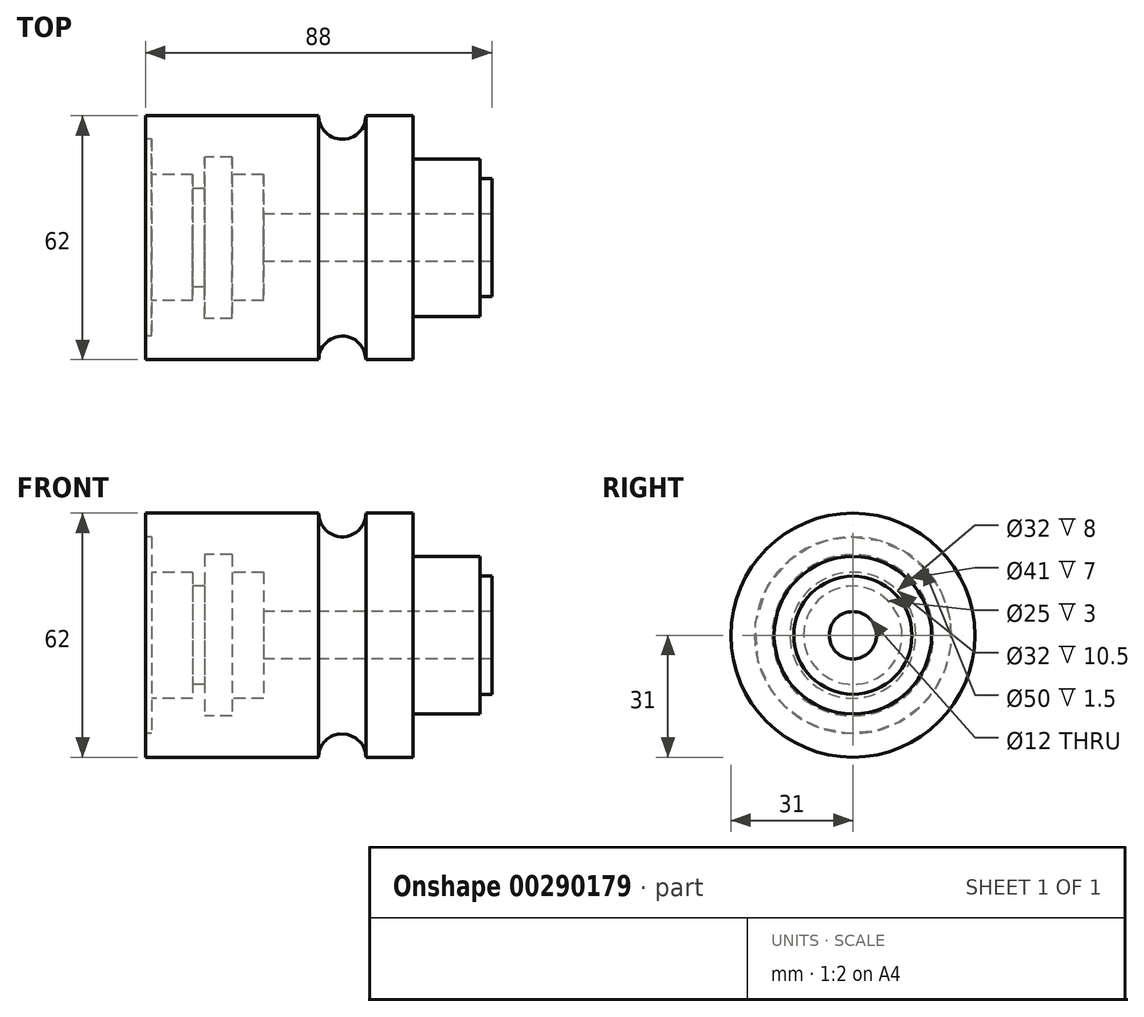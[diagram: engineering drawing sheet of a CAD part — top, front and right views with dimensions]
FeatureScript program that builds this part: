
annotation { "Feature Type Name" : "Feature", "Feature Type Description" : "" }
export const myFeature = defineFeature(function(context is Context, id is Id, definition is map)
    precondition{}
    {
        {
            var Q0;
            Q0=qCreatedBy(makeId("Front.planeOp"),FACE);
            var sketch = newSketch(context, id + "F0", { "sketchPlane" : qUnion([Q0])});
            skLineSegment(sketch, "E0", {"start": v(0, 0) * mm, "end": v(178.14, 0) * mm, "construction": true});
            skLineSegment(sketch, "E1", {"start": v(0, 0) * mm, "end": v(0, 31) * mm});
            skLineSegment(sketch, "E2", {"start": v(0, 31) * mm, "end": v(44, 31) * mm});
            skLineSegment(sketch, "E3", {"start": v(68, 31) * mm, "end": v(68, 20) * mm});
            skLineSegment(sketch, "E4", {"start": v(88, 15) * mm, "end": v(88, 0) * mm});
            skLineSegment(sketch, "E5", {"start": v(88, 0) * mm, "end": v(0, 0) * mm});
            skLineSegment(sketch, "E6", {"start": v(68, 20) * mm, "end": v(85, 20) * mm});
            skLineSegment(sketch, "E7", {"start": v(85, 20) * mm, "end": v(85, 15) * mm});
            skLineSegment(sketch, "E8", {"start": v(85, 15) * mm, "end": v(88, 15) * mm});
            skArc(sketch, "E9", {"start": v(44, 31) * mm, "mid": v(50, 25) * mm, "end": v(56, 31) * mm});
            skLineSegment(sketch, "E10.trimOffspring", {"start": v(56, 31) * mm, "end": v(68, 31) * mm});
            skSolve(sketch);
        }
        {
            var Q0;
            Q0 = qSketchRegion(id + "F0", true);
            var Q1;
            Q1=sQuery(id+"F0.wireOp",EDGE,"E0");
            revolve(context, id + "F1", {"entities" : qUnion([Q0]), "axis" : qUnion([Q1]), "revolveType" : RevolveType.FULL});
        }
        {
            var Q0;
            Q0=qCreatedBy(makeId("Front.planeOp"),FACE);
            var sketch = newSketch(context, id + "F2", { "sketchPlane" : qUnion([Q0])});
            skLineSegment(sketch, "E11", {"start": v(0, 0) * mm, "end": v(0, 25) * mm});
            skLineSegment(sketch, "E12", {"start": v(0, 25) * mm, "end": v(1.5, 25) * mm});
            skLineSegment(sketch, "E13", {"start": v(1.5, 25) * mm, "end": v(1.5, 16) * mm});
            skLineSegment(sketch, "E14", {"start": v(1.5, 16) * mm, "end": v(12, 16) * mm});
            skLineSegment(sketch, "E15", {"start": v(12, 16) * mm, "end": v(12, 12.5) * mm});
            skLineSegment(sketch, "E16", {"start": v(12, 12.5) * mm, "end": v(15, 12.5) * mm});
            skLineSegment(sketch, "E17", {"start": v(22, 16) * mm, "end": v(30, 16) * mm});
            skLineSegment(sketch, "E18", {"start": v(30, 16) * mm, "end": v(30, 6) * mm});
            skLineSegment(sketch, "E19", {"start": v(30, 6) * mm, "end": v(88, 6) * mm});
            skLineSegment(sketch, "E20", {"start": v(88, 6) * mm, "end": v(88, 0) * mm});
            skLineSegment(sketch, "E21", {"start": v(88, 0) * mm, "end": v(0, 0) * mm});
            skLineSegment(sketch, "E22", {"start": v(0, 0) * mm, "end": v(-52.04, 0) * mm, "construction": true});
            skLineSegment(sketch, "E23", {"start": v(15, 12.5) * mm, "end": v(15, 20.5) * mm});
            skLineSegment(sketch, "E24", {"start": v(15, 20.5) * mm, "end": v(22, 20.5) * mm});
            skLineSegment(sketch, "E25", {"start": v(22, 20.5) * mm, "end": v(22, 16) * mm});
            skSolve(sketch);
        }
        {
            var Q0;
            Q0 = qSketchRegion(id + "F2", true);
            var Q1;
            Q1=sQuery(id+"F2.wireOp",EDGE,"E22");
            revolve(context, id + "F3", {"operationType" : NewBodyOperationType.REMOVE, "entities" : qUnion([Q0]), "axis" : qUnion([Q1]), "revolveType" : RevolveType.FULL, "oppositeDirection" : true});
        }
    });
